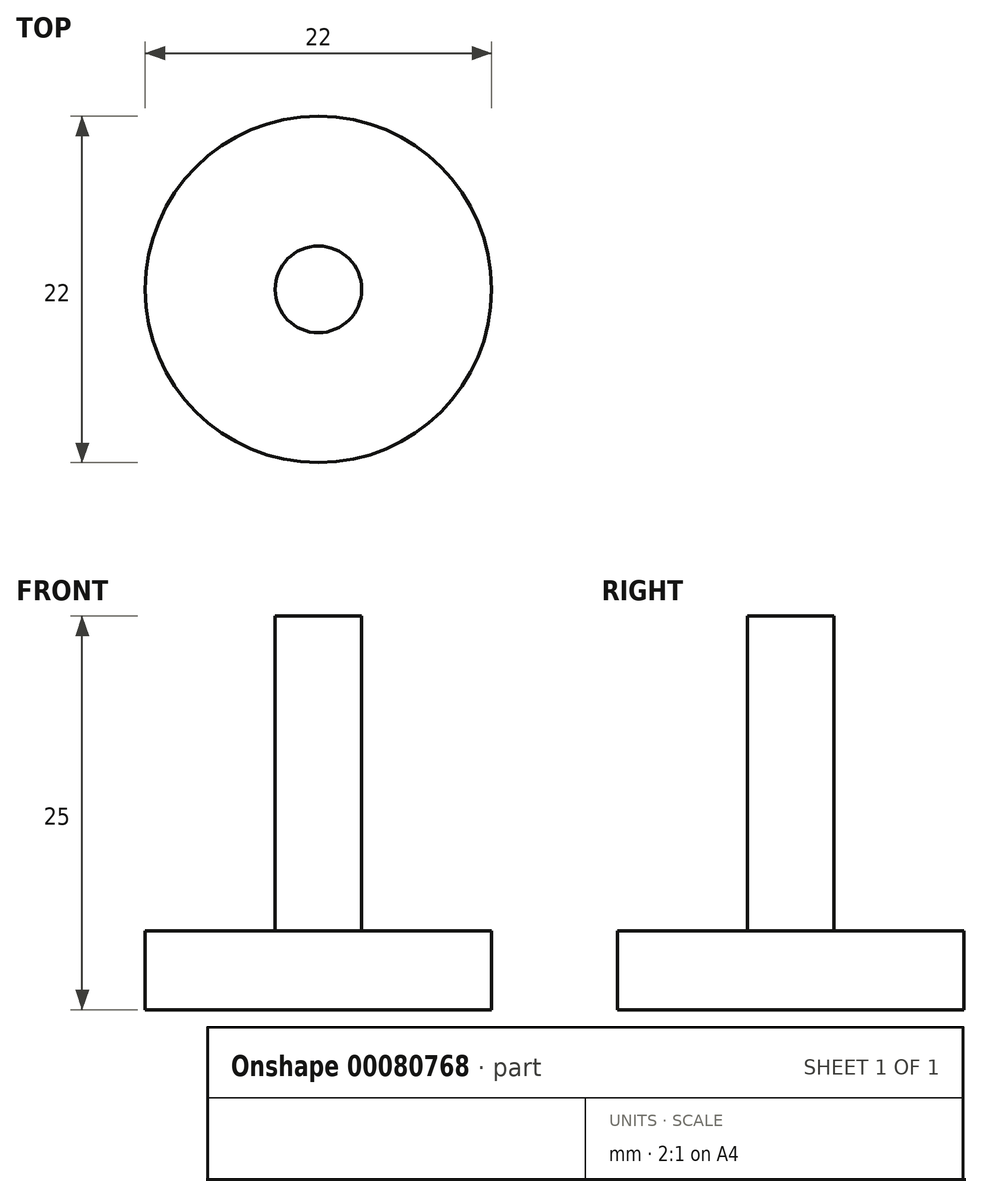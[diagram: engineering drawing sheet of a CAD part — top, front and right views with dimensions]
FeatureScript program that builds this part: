
annotation { "Feature Type Name" : "Feature", "Feature Type Description" : "" }
export const myFeature = defineFeature(function(context is Context, id is Id, definition is map)
    precondition{}
    {
        {
            var Q0;
            Q0=qCreatedBy(makeId("Top.planeOp"),FACE);
            var sketch = newSketch(context, id + "F0", { "sketchPlane" : qUnion([Q0])});
            skCircle(sketch, "E0", {"center": v(0, 0) * mm, "radius": 2.75 * mm});
            skCircle(sketch, "E1", {"center": v(0, 0) * mm, "radius": 11 * mm});
            skSolve(sketch);
        }
        {
            var Q0;
            Q0=makeQuery(id+"F0.imprint","IMPRINT",FACE,{"disambiguationData":[TD([[makeQuery(id+"F0.imprint","IMPRINT",EDGE,{"derivedFrom":sQuery(id+"F0.wireOp",EDGE,"E0")}),1.0]])]});
            extrude(context, id + "F1", {"entities" : qUnion([Q0]), "depth" : 25 * mm});
        }
        {
            var Q0;
            Q0 = qSketchRegion(id + "F0", true);
            extrude(context, id + "F2", {"entities" : qUnion([Q0]), "operationType" : NewBodyOperationType.ADD, "depth" : 5 * mm});
        }
    });
